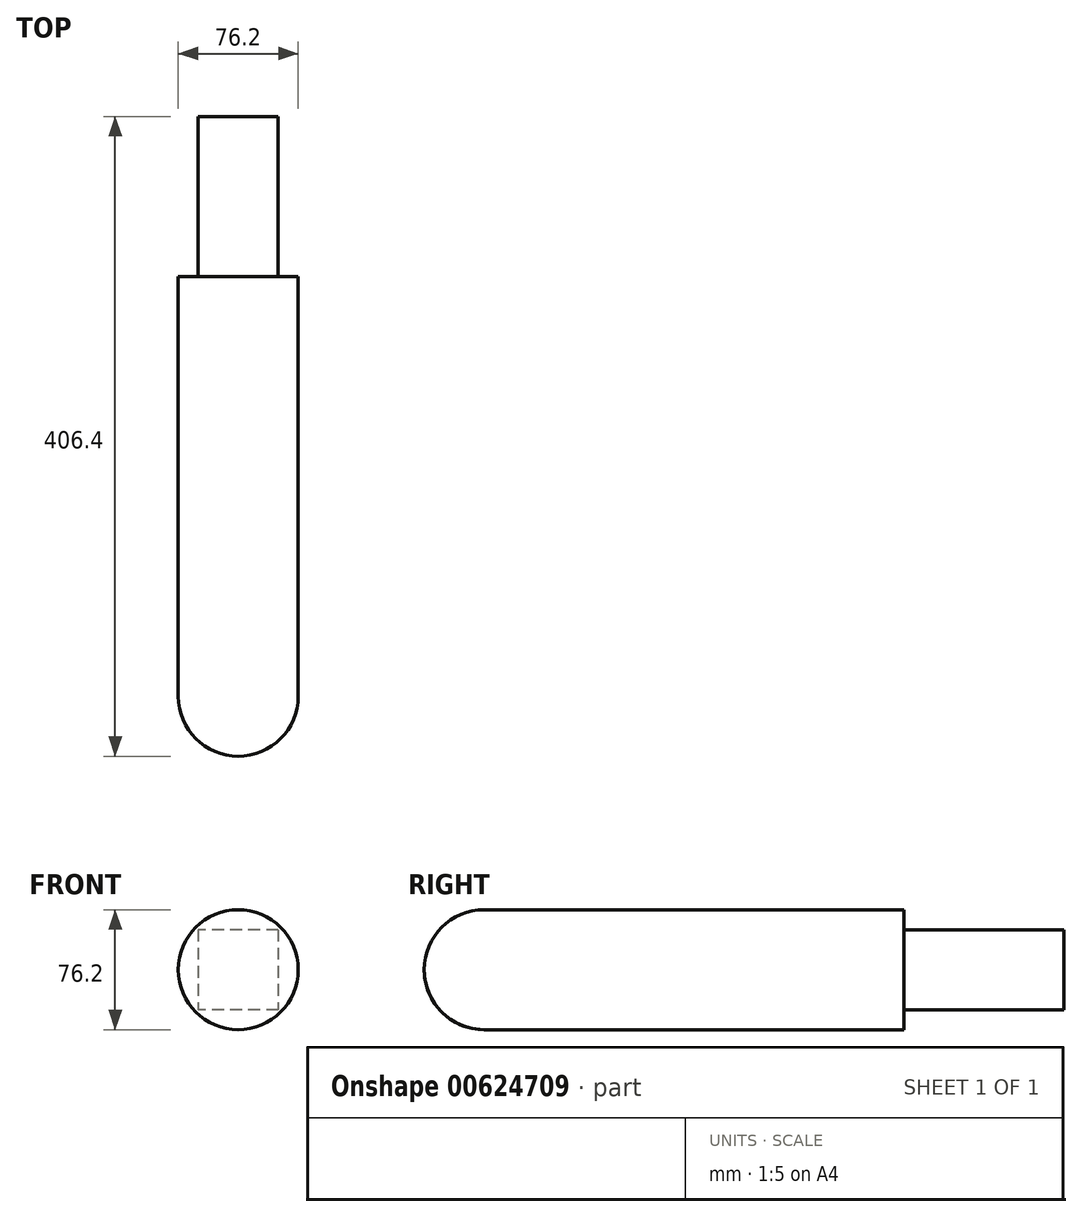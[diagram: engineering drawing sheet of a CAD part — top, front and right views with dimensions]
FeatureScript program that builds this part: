
annotation { "Feature Type Name" : "Feature", "Feature Type Description" : "" }
export const myFeature = defineFeature(function(context is Context, id is Id, definition is map)
    precondition{}
    {
        {
            var Q0;
            Q0=qCreatedBy(makeId("Front.planeOp"),FACE);
            var sketch = newSketch(context, id + "F0", { "sketchPlane" : qUnion([Q0])});
            skLineSegment(sketch, "E0.bottom", {"start": v(25.4, 25.4) * mm, "end": v(-25.4, 25.4) * mm});
            skLineSegment(sketch, "E0.top", {"start": v(25.4, -25.4) * mm, "end": v(-25.4, -25.4) * mm});
            skLineSegment(sketch, "E0.left", {"start": v(25.4, 25.4) * mm, "end": v(25.4, -25.4) * mm});
            skLineSegment(sketch, "E0.right", {"start": v(-25.4, 25.4) * mm, "end": v(-25.4, -25.4) * mm});
            skPoint(sketch, "E0.middle", {"position": v(0, 0) * mm});
            skSolve(sketch);
        }
        {
            var Q0;
            Q0 = qSketchRegion(id + "F0", true);
            extrude(context, id + "F1", {"entities" : qUnion([Q0]), "depth" : 101.6 * mm, "offsetDistance" : 25.4 * mm});
        }
        {
            var Q0;
            Q0=makeQuery(id+"F1.opExtrude","CAP_FACE",FACE,{"disambiguationData":[OSD([sQuery(id+"F0.wireOp",EDGE,"E0.bottom"),sQuery(id+"F0.wireOp",EDGE,"E0.top"),sQuery(id+"F0.wireOp",EDGE,"E0.left"),sQuery(id+"F0.wireOp",EDGE,"E0.right")])],"isStart":false});
            var sketch = newSketch(context, id + "F2", { "sketchPlane" : qUnion([Q0])});
            skCircle(sketch, "E1", {"center": v(0, 0) * mm, "radius": 38.1 * mm});
            skSolve(sketch);
        }
        {
            var Q0;
            Q0=makeQuery(id+"F2.imprint","IMPRINT",FACE,{"disambiguationData":[TD([[makeQuery(id+"F2.imprint","IMPRINT",EDGE,{"derivedFrom":makeQuery(id+"F1.opExtrude","CAP_EDGE",EDGE,{"disambiguationData":[OSD([sQuery(id+"F0.wireOp",EDGE,"E0.bottom")])],"isStart":false})}),1.0]])]});
            var Q1;
            Q1=makeQuery(id+"F2.imprint","IMPRINT",FACE,{"disambiguationData":[TD([[makeQuery(id+"F2.imprint","IMPRINT",EDGE,{"derivedFrom":sQuery(id+"F2.wireOp",EDGE,"E1")}),1.0]])]});
            extrude(context, id + "F3", {"entities" : qUnion([Q0, Q1]), "operationType" : NewBodyOperationType.ADD, "depth" : 304.8 * mm, "offsetDistance" : 25.4 * mm});
        }
        {
            var Q0;
            Q0=makeQuery(id+"F3.opExtrude","CAP_EDGE",EDGE,{"disambiguationData":[OSD([sQuery(id+"F2.wireOp",EDGE,"E1")])],"isStart":false});
            fillet(context, id + "F4", {"entities" : qUnion([Q0]), "radius" : 38.1 * mm, "tangentPropagation" : true, "allowEdgeOverflow" : false});
        }
    });
